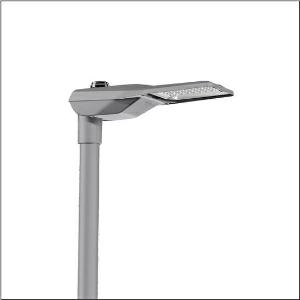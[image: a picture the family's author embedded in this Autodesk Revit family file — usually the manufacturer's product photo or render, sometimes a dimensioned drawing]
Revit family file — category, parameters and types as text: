
# Revit family: streetlight_sl_21_mini___st0_5a_5xe6b47n08hb_7d81
name_source: partatom
category: Lighting Fixtures
units: mm (PartAtom-declared; Revit-internal decimal feet)

## family parameters
Cut with Voids When Loaded = No
Host = Face
Light Source = No
Part Type = Normal
Room Calculation Point = No
Round Connector Dimension = Use Diameter
Shared = No

## types (1)
- --- (1 x LED, 9430 lm, 66 W, 4000K)
    Apparent Load = 66 VA
    CIE Flux Codes = 41 75 97 100 100
    Color Rendering = 70
    Color Temperature = 4000K
    Default Elevation = 1800 mm
    Description = Streetlight SL 21 mini, mast luminaire, primary light control with lens, of PMMA, primary optical cover: cover, of toughened safety glass, transparent, light distribution: ST0.5a, light emission: direct distribution, primary light characteristic: asymmetric, installation type: side-entry, LED, 3G 1.5mm², High Power LED, rated luminous flux: 9.430lm, luminous efficacy: 143lm/W, light colour: 740, colour temperature: 4000K, control gear: NEMA (7pin), control: overheat protection, pre-setting: linear dimming characteristic, constant luminous flux control, time-dependent luminous flux control, flexible luminous flux parameterisation, mains connection: 230..240V, AC, 50/60Hz, connection cable pre-assembled, cable length: 8,5m, wiring characteristics: H07RN-F, start of lifetime: 66W, end of service life: 69W, reduction: 30W, luminaire housing, of diecast aluminium (EN AC-44300), powder-coated, Siteco® metallic grey (DB 702S), corrosivity category C5 mid according to DIN EN ISO 12944, multi-level sealing system, sealing non-destructively replaceable, inclination adjustable: 0°, 5°, 10°, 15°, length: 628mm, width: 235mm, height: 110mm, spigot size: 42mm (side-entry), mounting height: 4..8m, protection rating (complete): IP66, insulation class (complete): insulation class I (protective earthing), certification: CE, ENEC, ENEC+, VDE, impact resistance: IK09, permissible operating ambient temperature for outdoor applications: -40..+50°C, standard-compliant lighting for roads and squares, packaging unit: 1 piece

Light Distribution: ST0.5a
    Height = 110 mm
    Lamp = 1 x LED
    Lamp Light Flux = 9430 lm
    Lamp Power = 66 W
    Lamp count = 1
    Length = 625 mm
    Luminous efficacy = 143 lm/W
    Manufacturer = Siteco
    ModVariant = No
    Model = 5XE6B47N08HB
    Number of Poles = 1
    OnlyDefault = Yes
    Power Factor = 1
    Product Name = Streetlight SL 21 mini | ST0.5a
    Product group = mast luminaire | pylon top
    ProductGroupID = 6100
    Protection Class = Protection class I
    Protection Degree = IP 66
    RLX_Detail_Level = 1
    RLX_Emergency_Light_Flux = 0 lm
    RLX_Emergency_Type = 0
    RLX_Emergency_Type_DB = No
    RlxData = <blob elided: 103177 chars, md5=5c2e7195>
    Socket = socket
    Standby Power = 0 W
    System Light Flux = 9430 lm
    System Power = 66 W
    Type Comments = factory setting: luminous flux: 100 % | dim-lin: 254 | 670 mA
    Type Image = l_1294379.jpg
    URL = http://relux.com
    VarID = @adj_132724
    Voltage = 0 V
    Weight = 0.00 kg
    Width = 234 mm

## geometry (parser evidence)
native form markers: Blend x4, Sweep x9
no freeform markers — native parametric forms only
